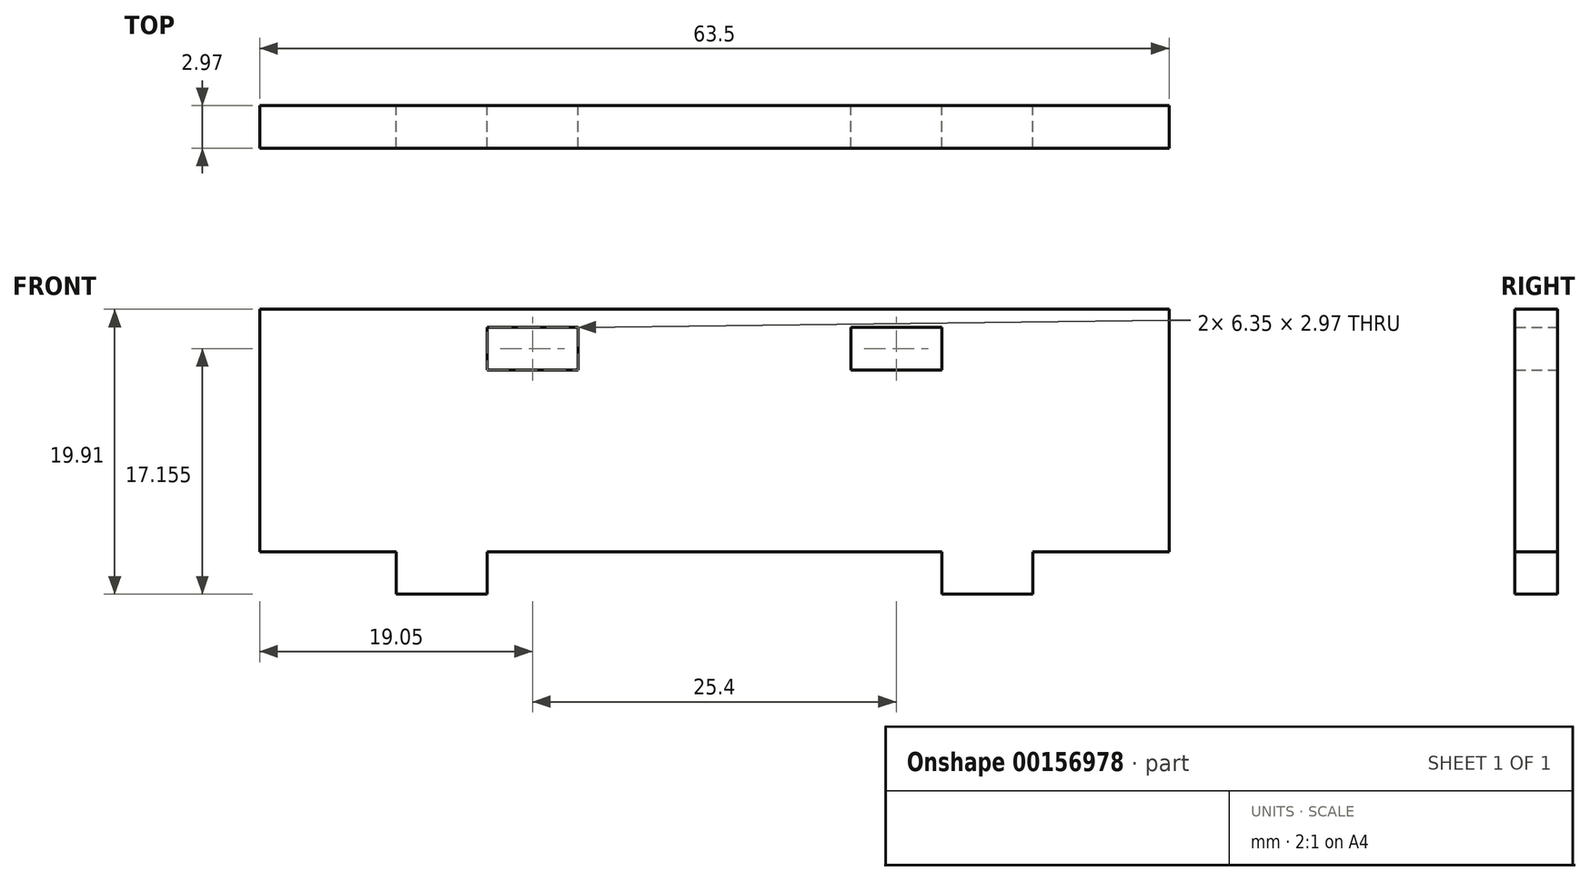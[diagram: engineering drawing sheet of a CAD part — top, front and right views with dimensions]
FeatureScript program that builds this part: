
annotation { "Feature Type Name" : "Feature", "Feature Type Description" : "" }
export const myFeature = defineFeature(function(context is Context, id is Id, definition is map)
    precondition{}
    {
        {
            var Q0;
            Q0=qCreatedBy(makeId("Front.planeOp"),FACE);
            var sketch = newSketch(context, id + "F0", { "sketchPlane" : qUnion([Q0])});
            skLineSegment(sketch, "E0.bottom", {"start": v(31.75, 8.47) * mm, "end": v(-31.75, 8.47) * mm});
            skLineSegment(sketch, "E0.top", {"start": v(31.75, -8.47) * mm, "end": v(-31.75, -8.47) * mm});
            skLineSegment(sketch, "E0.left", {"start": v(31.75, 8.47) * mm, "end": v(31.75, -8.47) * mm});
            skLineSegment(sketch, "E0.right", {"start": v(-31.75, 8.47) * mm, "end": v(-31.75, -8.47) * mm});
            skPoint(sketch, "E0.middle", {"position": v(0, 0) * mm});
            skLineSegment(sketch, "E1", {"start": v(0, 0) * mm, "end": v(0, 8.47) * mm, "construction": true});
            skLineSegment(sketch, "E2", {"start": v(0, 0) * mm, "end": v(0, -8.47) * mm, "construction": true});
            skLineSegment(sketch, "E3", {"start": v(0, 0) * mm, "end": v(-31.75, 0) * mm, "construction": true});
            skLineSegment(sketch, "E4", {"start": v(0, 0) * mm, "end": v(31.75, 0) * mm, "construction": true});
            skLineSegment(sketch, "E5.bottom", {"start": v(-9.53, 4.23) * mm, "end": v(-15.88, 4.23) * mm});
            skLineSegment(sketch, "E5.top", {"start": v(-9.53, 7.2) * mm, "end": v(-15.88, 7.2) * mm});
            skLineSegment(sketch, "E5.left", {"start": v(-9.53, 4.23) * mm, "end": v(-9.53, 7.2) * mm});
            skLineSegment(sketch, "E5.right", {"start": v(-15.88, 4.23) * mm, "end": v(-15.88, 7.2) * mm});
            skPoint(sketch, "E5.middle", {"position": v(-12.7, 5.72) * mm});
            skLineSegment(sketch, "E6.MirrorCS", {"start": v(9.52, 4.23) * mm, "end": v(15.88, 4.23) * mm});
            skLineSegment(sketch, "E7.MirrorCS", {"start": v(15.88, 4.23) * mm, "end": v(15.88, 7.2) * mm});
            skLineSegment(sketch, "E8.MirrorCS", {"start": v(9.52, 7.2) * mm, "end": v(15.88, 7.2) * mm});
            skLineSegment(sketch, "E9.MirrorCS", {"start": v(9.53, 4.23) * mm, "end": v(9.53, 7.2) * mm});
            skLineSegment(sketch, "E10.bottom", {"start": v(-15.88, -11.44) * mm, "end": v(-22.23, -11.44) * mm});
            skLineSegment(sketch, "E10.left", {"start": v(-15.88, -11.44) * mm, "end": v(-15.88, -8.47) * mm});
            skLineSegment(sketch, "E10.right", {"start": v(-22.23, -11.44) * mm, "end": v(-22.23, -8.47) * mm});
            skPoint(sketch, "E10.middle", {"position": v(-19.05, -8.47) * mm});
            skLineSegment(sketch, "E11.MirrorCS", {"start": v(22.23, -11.44) * mm, "end": v(22.23, -8.47) * mm});
            skLineSegment(sketch, "E12.MirrorCS", {"start": v(15.88, -11.44) * mm, "end": v(15.88, -8.47) * mm});
            skLineSegment(sketch, "E13.MirrorCS", {"start": v(15.88, -11.44) * mm, "end": v(22.23, -11.44) * mm});
            skPoint(sketch, "E14.orphan", {"position": v(15.88, -5.5) * mm});
            skPoint(sketch, "E15.orphan", {"position": v(22.23, -5.5) * mm});
            skPoint(sketch, "E16.orphan", {"position": v(-22.23, -5.5) * mm});
            skPoint(sketch, "E17.orphan", {"position": v(-15.88, -5.5) * mm});
            skSolve(sketch);
        }
        {
            var Q0;
            Q0 = qSketchRegion(id + "F0", true);
            extrude(context, id + "F1", {"entities" : qUnion([Q0]), "depth" : 2.97 * mm});
        }
    });
